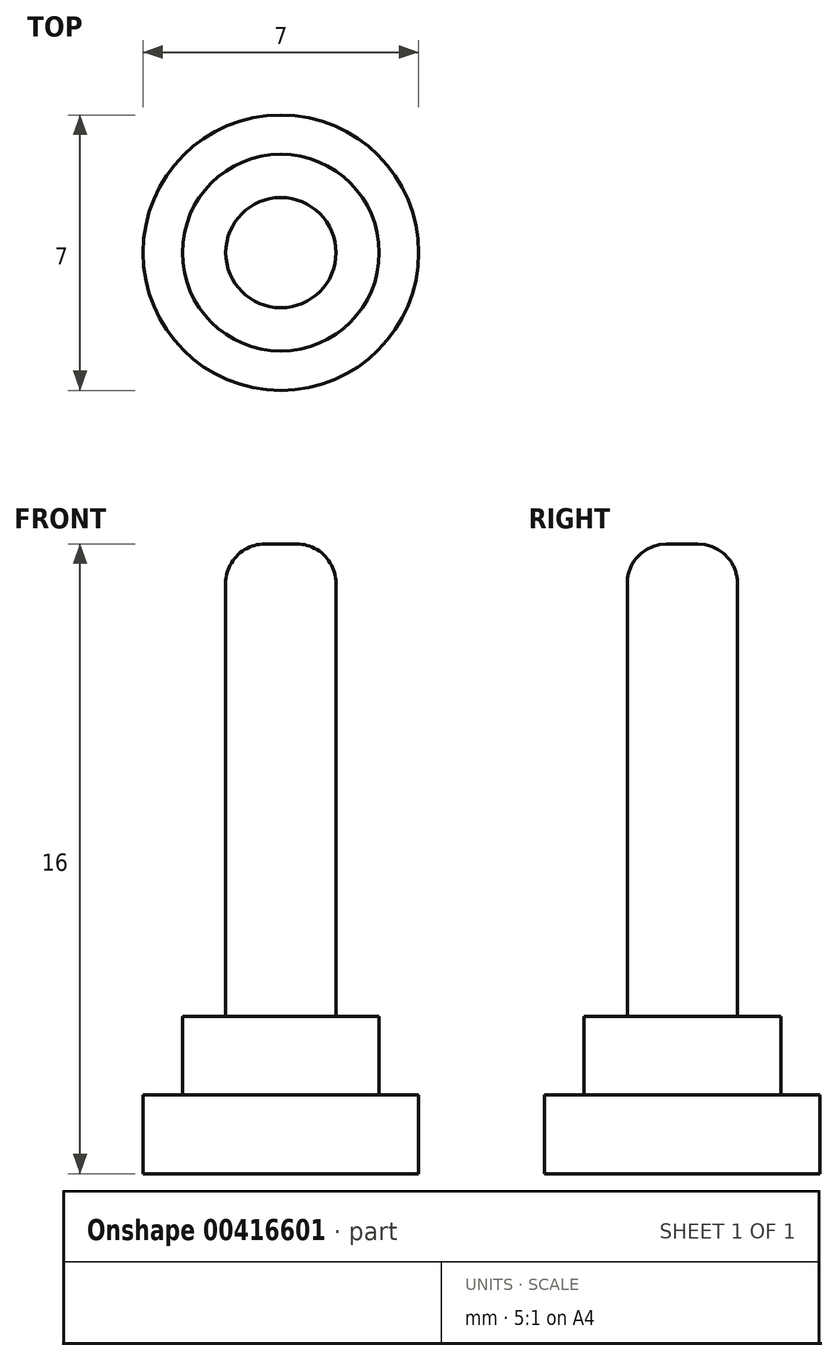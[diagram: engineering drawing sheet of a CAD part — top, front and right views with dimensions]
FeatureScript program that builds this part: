
annotation { "Feature Type Name" : "Feature", "Feature Type Description" : "" }
export const myFeature = defineFeature(function(context is Context, id is Id, definition is map)
    precondition{}
    {
        {
            var Q0;
            Q0=qCreatedBy(makeId("Top.planeOp"),FACE);
            var sketch = newSketch(context, id + "F0", { "sketchPlane" : qUnion([Q0])});
            skCircle(sketch, "E0", {"center": v(0, 0) * mm, "radius": 3.5 * mm});
            skSolve(sketch);
        }
        {
            var Q0;
            Q0 = qSketchRegion(id + "F0", true);
            extrude(context, id + "F1", {"entities" : qUnion([Q0]), "depth" : 2 * mm});
        }
        {
            var Q0;
            Q0=makeQuery(id+"F1.opExtrude","CAP_FACE",FACE,{"disambiguationData":[OSD([sQuery(id+"F0.wireOp",EDGE,"E0")])],"isStart":false});
            var sketch = newSketch(context, id + "F2", { "sketchPlane" : qUnion([Q0])});
            skCircle(sketch, "E1", {"center": v(0, 0) * mm, "radius": 2.5 * mm});
            skSolve(sketch);
        }
        {
            var Q0;
            Q0=makeQuery(id+"F2.imprint","IMPRINT",FACE,{"disambiguationData":[TD([[makeQuery(id+"F2.imprint","IMPRINT",EDGE,{"derivedFrom":sQuery(id+"F2.wireOp",EDGE,"E1")}),1.0]])]});
            extrude(context, id + "F3", {"entities" : qUnion([Q0]), "operationType" : NewBodyOperationType.ADD, "depth" : 2 * mm});
        }
        {
            var Q0;
            Q0=makeQuery(id+"F3.opExtrude","CAP_FACE",FACE,{"disambiguationData":[OSD([sQuery(id+"F2.wireOp",EDGE,"E1")])],"isStart":false});
            var sketch = newSketch(context, id + "F4", { "sketchPlane" : qUnion([Q0])});
            skCircle(sketch, "E2", {"center": v(0, 0) * mm, "radius": 1.4 * mm});
            skSolve(sketch);
        }
        {
            var Q0;
            Q0=makeQuery(id+"F4.imprint","IMPRINT",FACE,{"disambiguationData":[TD([[makeQuery(id+"F4.imprint","IMPRINT",EDGE,{"derivedFrom":sQuery(id+"F4.wireOp",EDGE,"E2")}),1.0]])]});
            var Q1;
            Q1=sQuery(id+"F4.wireOp",EDGE,"E2");
            extrude(context, id + "F5", {"entities" : qUnion([Q0]), "surfaceEntities" : qUnion([Q1]), "depth" : 12 * mm});
        }
        {
            var Q0;
            Q0=makeQuery(id+"F5.opExtrude","CAP_EDGE",EDGE,{"disambiguationData":[OSD([sQuery(id+"F4.wireOp",EDGE,"E2")])],"isStart":false});
            fillet(context, id + "F6", {"entities" : qUnion([Q0]), "radius" : 1 * mm, "tangentPropagation" : true, "allowEdgeOverflow" : false});
        }
    });
